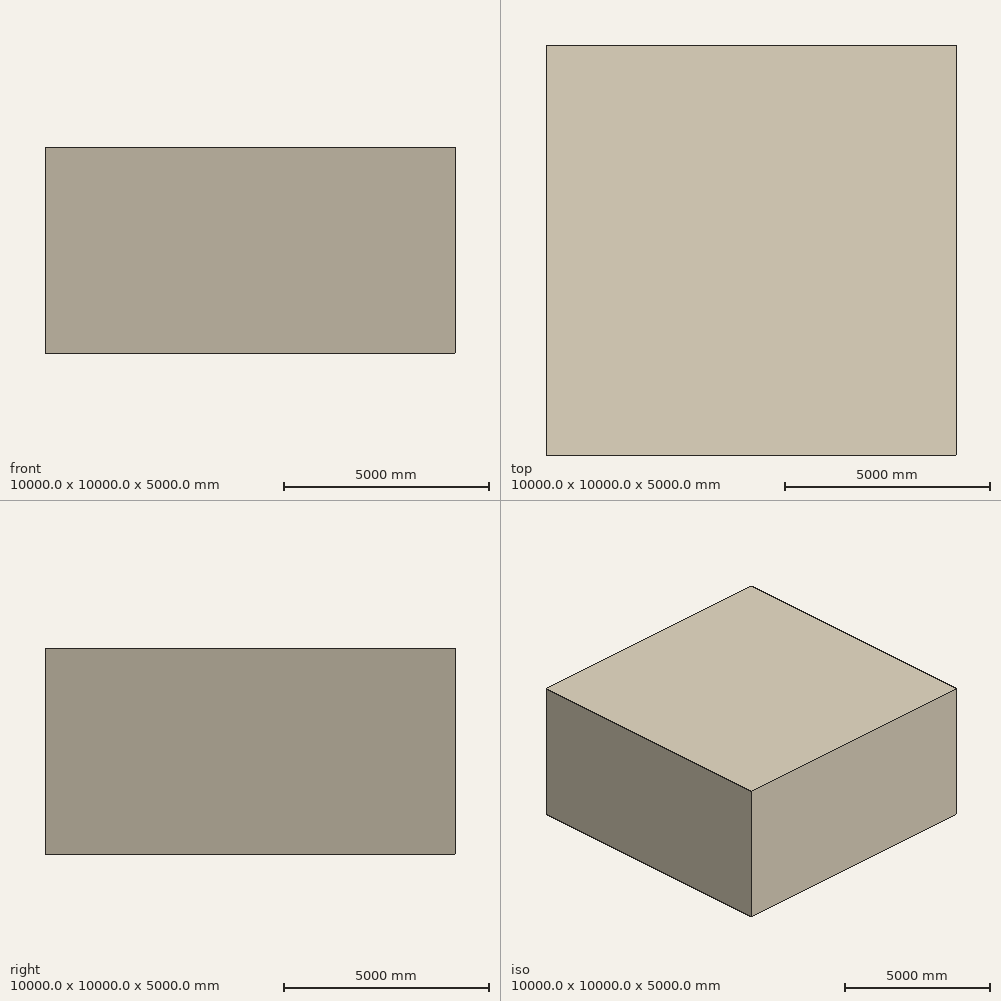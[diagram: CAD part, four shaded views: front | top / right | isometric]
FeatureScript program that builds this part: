
annotation { "Feature Type Name" : "Feature", "Feature Type Description" : "" }
export const myFeature = defineFeature(function(context is Context, id is Id, definition is map)
    precondition{}
    {
        {
            var Q0;
            Q0=qCreatedBy(makeId("Front.planeOp"),FACE);
            var sketch = newSketch(context, id + "F0", { "sketchPlane" : qUnion([Q0])});
            skLineSegment(sketch, "E0.bottom", {"start": v(5000, 2500) * mm, "end": v(-5000, 2500) * mm});
            skLineSegment(sketch, "E0.top", {"start": v(5000, -2500) * mm, "end": v(-5000, -2500) * mm});
            skLineSegment(sketch, "E0.left", {"start": v(5000, 2500) * mm, "end": v(5000, -2500) * mm});
            skLineSegment(sketch, "E0.right", {"start": v(-5000, 2500) * mm, "end": v(-5000, -2500) * mm});
            skPoint(sketch, "E0.middle", {"position": v(0, 0) * mm});
            skSolve(sketch);
        }
        {
            var Q0;
            Q0=makeQuery(id+"F0.imprint","IMPRINT",FACE,{"disambiguationData":[TD([[makeQuery(id+"F0.imprint","IMPRINT",EDGE,{"derivedFrom":sQuery(id+"F0.wireOp",EDGE,"E0.bottom")}),1.0]])]});
            extrude(context, id + "F1", {"entities" : qUnion([Q0]), "endBound" : BoundingType.SYMMETRIC, "depth" : 10000 * mm, "offsetDistance" : 25 * mm});
        }
    });
